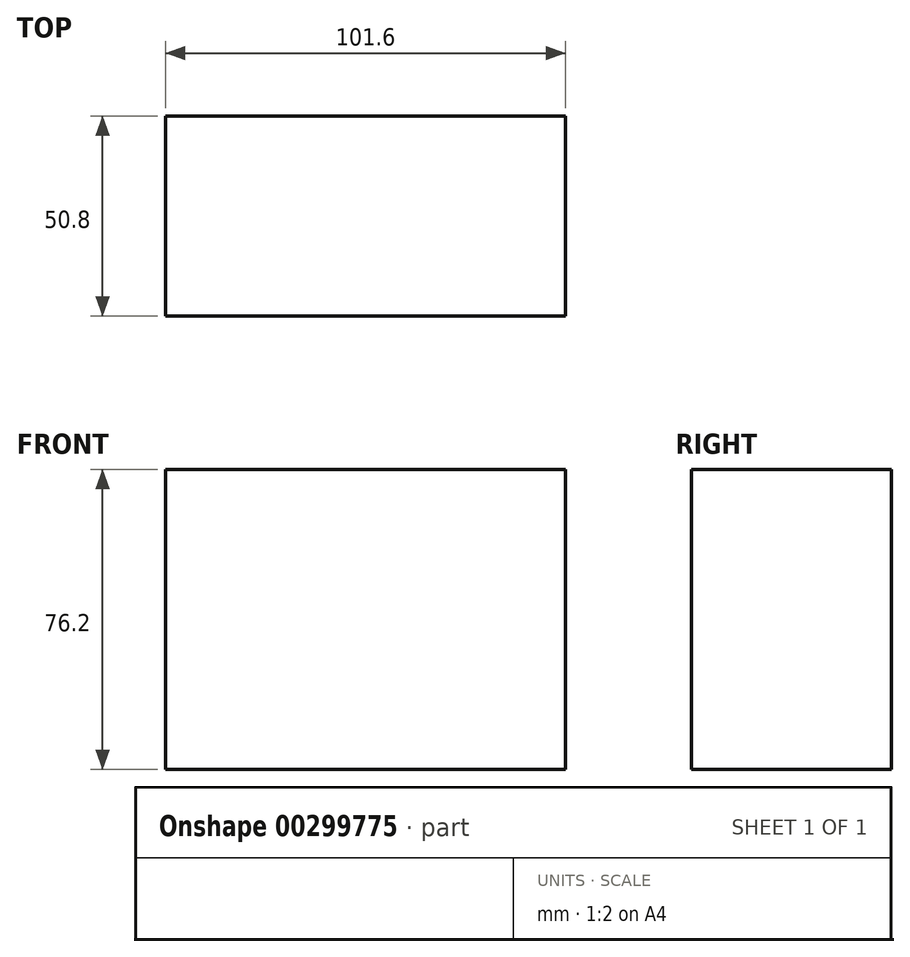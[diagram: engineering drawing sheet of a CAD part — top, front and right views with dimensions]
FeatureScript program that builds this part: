
annotation { "Feature Type Name" : "Feature", "Feature Type Description" : "" }
export const myFeature = defineFeature(function(context is Context, id is Id, definition is map)
    precondition{}
    {
        {
            var Q0;
            Q0=qCreatedBy(makeId("Front.planeOp"),FACE);
            var sketch = newSketch(context, id + "F0", { "sketchPlane" : qUnion([Q0])});
            skLineSegment(sketch, "E0.bottom", {"start": v(50.8, 38.1) * mm, "end": v(-50.8, 38.1) * mm});
            skLineSegment(sketch, "E0.top", {"start": v(50.8, -38.1) * mm, "end": v(-50.8, -38.1) * mm});
            skLineSegment(sketch, "E0.left", {"start": v(50.8, 38.1) * mm, "end": v(50.8, -38.1) * mm});
            skLineSegment(sketch, "E0.right", {"start": v(-50.8, 38.1) * mm, "end": v(-50.8, -38.1) * mm});
            skPoint(sketch, "E0.middle", {"position": v(0, 0) * mm});
            skSolve(sketch);
        }
        {
            var Q0;
            Q0 = qSketchRegion(id + "F0", true);
            extrude(context, id + "F1", {"entities" : qUnion([Q0]), "depth" : 50.8 * mm});
        }
    });
